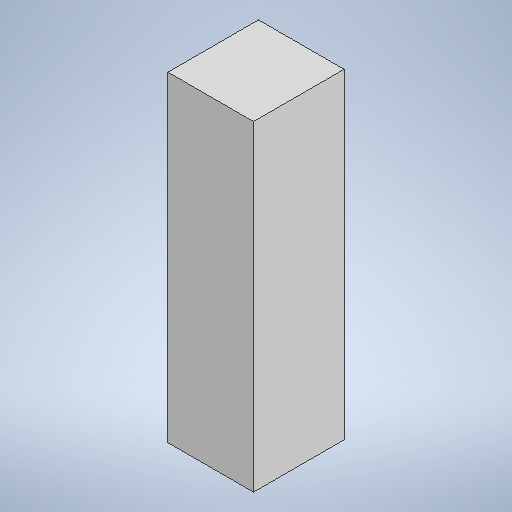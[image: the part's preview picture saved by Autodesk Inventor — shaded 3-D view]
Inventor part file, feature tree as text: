
AUTODESK INVENTOR PART (.ipt)
format: ipt  version: 2025.2 (Build 292293000, 293)  size: 224,256 bytes
history: native  units: in
note: dims shown in document units (in); Inventor stores cm internally (conversion verified against a paired STEP export)
features: extrude x2, sketch x2, other x1
ambient origin geometry x8: Origin, YZ Plane, XZ Plane, XY Plane, X Axis, Y Axis, Z Axis, Center Point
bodies: Solid1 (feature_tree)
feature tree (5):
  other  "EndCap"
  extrude  "Extrusion1"  Depth=0.5in TaperAngle=0.0deg
  extrude  "Extrusion3"  Depth=0.25in
  sketch  "Sketch1"  dims[d0=0.4724in d1=1.7717in d2=2.2658in d3=0.5in d4=0.0in]
  sketch  "Sketch3"  dims[d10=0.25in d11=0.25in d12=0.25in d13=0.25in d14=0.25in d15=0.25in d16=0.25in d17=0.0in]
